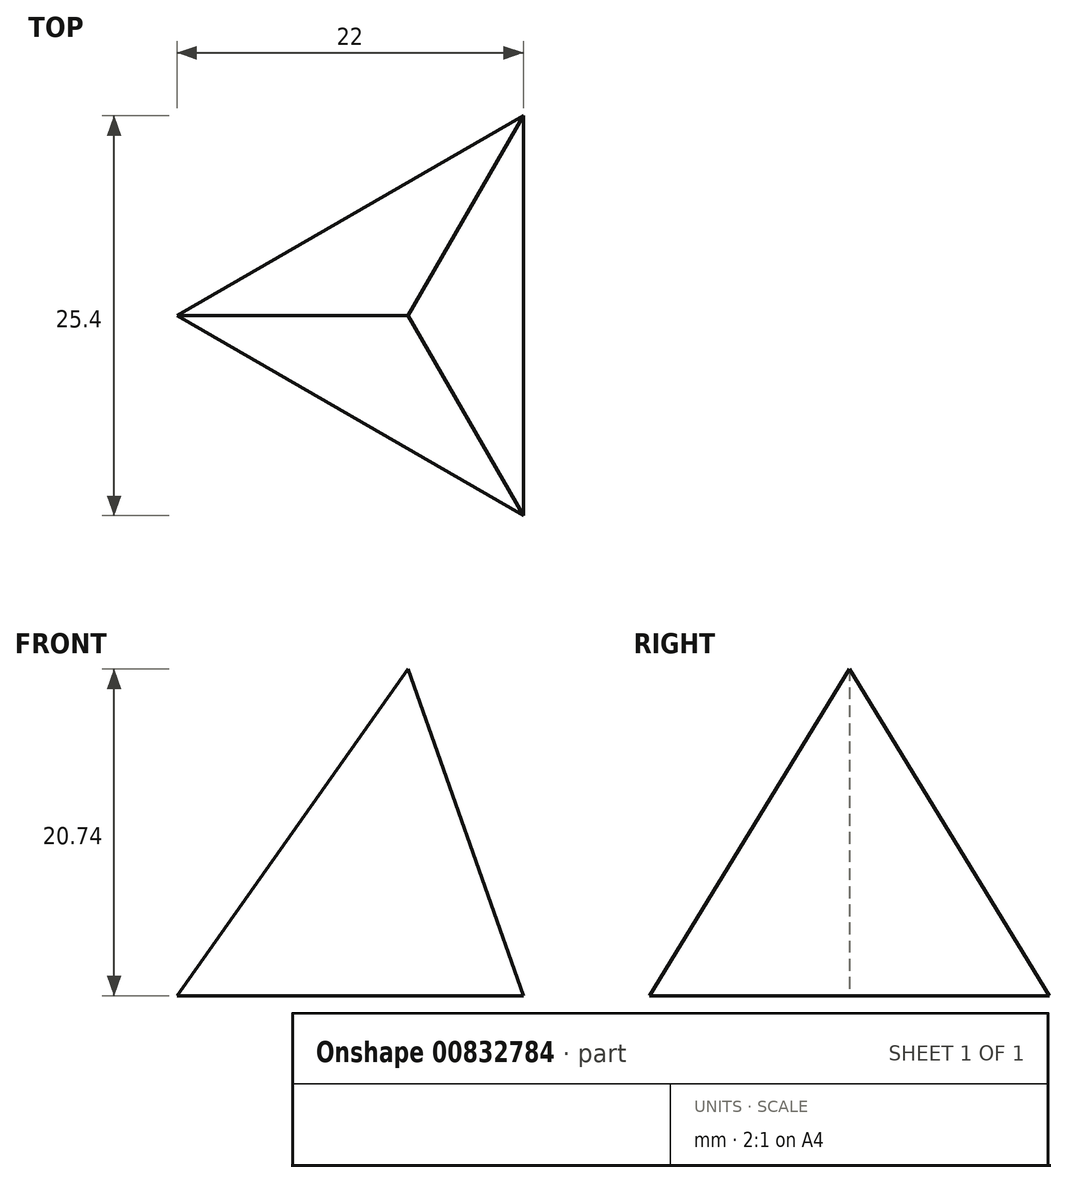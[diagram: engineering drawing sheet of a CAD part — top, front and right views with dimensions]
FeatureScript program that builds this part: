
annotation { "Feature Type Name" : "Feature", "Feature Type Description" : "" }
export const myFeature = defineFeature(function(context is Context, id is Id, definition is map)
    precondition{}
    {
        {
            var Q0;
            Q0=qCreatedBy(makeId("Top.planeOp"),FACE);
            var sketch = newSketch(context, id + "F0", { "sketchPlane" : qUnion([Q0])});
            skLineSegment(sketch, "E0", {"start": v(0, 0) * mm, "end": v(0, -12.7) * mm});
            skLineSegment(sketch, "E1", {"start": v(0, -12.7) * mm, "end": v(-22, 0) * mm});
            skLineSegment(sketch, "E2", {"start": v(-22, 0) * mm, "end": v(0, 0) * mm});
            skPoint(sketch, "E3", {"position": v(-22, 0) * mm});
            skLineSegment(sketch, "E4", {"start": v(-22, 0) * mm, "end": v(0, 12.7) * mm});
            skLineSegment(sketch, "E5", {"start": v(0, 12.7) * mm, "end": v(0, 0) * mm});
            skLineSegment(sketch, "E6", {"start": v(0, -12.7) * mm, "end": v(-11, 6.35) * mm});
            skPoint(sketch, "E7", {"position": v(-7.33, 0) * mm});
            skSolve(sketch);
        }
        {
            var Q0;
            Q0=qCreatedBy(makeId("Front.planeOp"),FACE);
            var sketch = newSketch(context, id + "F1", { "sketchPlane" : qUnion([Q0])});
            skLineSegment(sketch, "E8", {"start": v(0, 0) * mm, "end": v(-22, 0) * mm});
            skLineSegment(sketch, "E9", {"start": v(-22, 0) * mm, "end": v(-7.33, 20.74) * mm});
            skLineSegment(sketch, "E10", {"start": v(-7.33, 0) * mm, "end": v(-7.33, 20.74) * mm});
            skLineSegment(sketch, "E11", {"start": v(-7.33, 20.74) * mm, "end": v(0, 0) * mm});
            skSolve(sketch);
        }
        {
            var Q0;
            Q0=sQuery(id+"F1.wireOp",VERTEX,"E9.end");
            var Q1;
            Q1=sQuery(id+"F0.wireOp",VERTEX,"E0.end");
            var Q2;
            Q2=sQuery(id+"F0.wireOp",VERTEX,"E0.start");
            cPlane(context, id + "F2", {"entities" : qUnion([Q0, Q1, Q2]), "cplaneType" : CPlaneType.THREE_POINT, "offset" : 25.4 * mm, "width" : 152.4 * mm, "height" : 152.4 * mm});
        }
        {
            var Q0;
            Q0=qCreatedBy(id+"F2.planeOp",FACE);
            var sketch = newSketch(context, id + "F3", { "sketchPlane" : qUnion([Q0])});
            skLineSegment(sketch, "E12", {"start": v(0, 0) * mm, "end": v(0, 22) * mm});
            skLineSegment(sketch, "E13", {"start": v(0, 22) * mm, "end": v(12.7, 0) * mm});
            skLineSegment(sketch, "E14", {"start": v(12.7, 0) * mm, "end": v(0, 0) * mm});
            skLineSegment(sketch, "E15", {"start": v(0, 22) * mm, "end": v(-12.7, 0) * mm});
            skLineSegment(sketch, "E16", {"start": v(-12.7, 0) * mm, "end": v(0, 0) * mm});
            skPoint(sketch, "E17", {"position": v(0, 22) * mm});
            skSolve(sketch);
        }
        {
            var Q0;
            Q0 = qSketchRegion(id + "F0", true);
            extrude(context, id + "F4", {"entities" : qUnion([Q0]), "depth" : 25.4 * mm, "offsetDistance" : 25.4 * mm});
        }
        {
            var Q0;
            Q0=qCreatedBy(id+"F2.planeOp",FACE);
            var sketch = newSketch(context, id + "F5", { "sketchPlane" : qUnion([Q0])});
            skLineSegment(sketch, "E18.bottom", {"start": v(19.29, -4.86) * mm, "end": v(-27.31, -4.86) * mm});
            skLineSegment(sketch, "E18.top", {"start": v(19.29, 34.9) * mm, "end": v(-27.31, 34.9) * mm});
            skLineSegment(sketch, "E18.left", {"start": v(19.29, -4.86) * mm, "end": v(19.29, 34.9) * mm});
            skLineSegment(sketch, "E18.right", {"start": v(-27.31, -4.86) * mm, "end": v(-27.31, 34.9) * mm});
            skSolve(sketch);
        }
        {
            var Q0;
            Q0 = qSketchRegion(id + "F5", true);
            extrude(context, id + "F6", {"entities" : qUnion([Q0]), "operationType" : NewBodyOperationType.REMOVE, "oppositeDirection" : true, "depth" : 25.4 * mm, "offsetDistance" : 25.4 * mm});
        }
        {
            var Q0;
            Q0=sQuery(id+"F1.wireOp",VERTEX,"E9.end");
            var Q1;
            Q1=sQuery(id+"F3.wireOp",VERTEX,"E13.end");
            var Q2;
            Q2=sQuery(id+"F1.wireOp",VERTEX,"E8.end");
            cPlane(context, id + "F7", {"entities" : qUnion([Q0, Q1, Q2]), "cplaneType" : CPlaneType.THREE_POINT, "offset" : 25.4 * mm, "width" : 152.4 * mm, "height" : 152.4 * mm});
        }
        {
            var Q0;
            Q0=qCreatedBy(id+"F7.planeOp",FACE);
            var sketch = newSketch(context, id + "F8", { "sketchPlane" : qUnion([Q0])});
            skLineSegment(sketch, "E19.bottom", {"start": v(-33.53, -9.72) * mm, "end": v(34.55, -9.72) * mm});
            skLineSegment(sketch, "E19.top", {"start": v(-33.53, 41.05) * mm, "end": v(34.55, 41.05) * mm});
            skLineSegment(sketch, "E19.left", {"start": v(-33.53, -9.72) * mm, "end": v(-33.53, 41.05) * mm});
            skLineSegment(sketch, "E19.right", {"start": v(34.55, -9.72) * mm, "end": v(34.55, 41.05) * mm});
            skSolve(sketch);
        }
        {
            var Q0;
            Q0 = qSketchRegion(id + "F8", true);
            extrude(context, id + "F9", {"entities" : qUnion([Q0]), "operationType" : NewBodyOperationType.REMOVE, "depth" : 25.4 * mm, "offsetDistance" : 25.4 * mm});
        }
        {
            var Q0;
            Q0=sQuery(id+"F3.wireOp",VERTEX,"E17");
            var Q1;
            Q1=sQuery(id+"F1.wireOp",VERTEX,"E8.end");
            var Q2;
            Q2=sQuery(id+"F3.wireOp",VERTEX,"E15.end");
            cPlane(context, id + "F10", {"entities" : qUnion([Q0, Q1, Q2]), "cplaneType" : CPlaneType.THREE_POINT, "offset" : 25.4 * mm, "width" : 152.4 * mm, "height" : 152.4 * mm});
        }
        {
            var Q0;
            Q0=qCreatedBy(id+"F10.planeOp",FACE);
            var sketch = newSketch(context, id + "F11", { "sketchPlane" : qUnion([Q0])});
            skLineSegment(sketch, "E20.bottom", {"start": v(-11.77, -12.45) * mm, "end": v(33.85, -12.45) * mm});
            skLineSegment(sketch, "E20.top", {"start": v(-11.77, 45.72) * mm, "end": v(33.85, 45.72) * mm});
            skLineSegment(sketch, "E20.left", {"start": v(-11.77, -12.45) * mm, "end": v(-11.77, 45.72) * mm});
            skLineSegment(sketch, "E20.right", {"start": v(33.85, -12.45) * mm, "end": v(33.85, 45.72) * mm});
            skSolve(sketch);
        }
        {
            var Q0;
            Q0 = qSketchRegion(id + "F11", true);
            extrude(context, id + "F12", {"entities" : qUnion([Q0]), "operationType" : NewBodyOperationType.REMOVE, "depth" : 25.4 * mm, "offsetDistance" : 25.4 * mm});
        }
    });
